# Revit family: Sanitary_Toilet-Accessories_DURAVIT-AG_ME-by-Starck-Siphon-cover-085840ed
name_source: partatom
category: Specialty Equipment
revit_build: Autodesk Revit 2018 (Build: 20190510_1515(x64)
units: mm (PartAtom-declared; Revit-internal decimal feet)

## family parameters
Cut with Voids When Loaded = No
Host = Face
OmniClass Number = 23.19.31.17
OmniClass Title = Sanitary Room Units
Part Type = Normal
Room Calculation Point = No
Round Connector Dimension = Use Diameter
Shared = No

## types (2) — shared parameters
BIMobject category = Toilet Accessories
Date of publishing = 11.01.2017 00:00:00
Default Elevation = 1219 mm
ETIM classification = EC011331 | Siphon cover
Edition number = 1
IFC Classification = Sanitary Terminal
Installation instructions = http://pro.duravit.com
Manufacturer = Duravit
Manufacturer country = France
Manufacturer name = DURAVIT AG
Masterformat 2014 Code = 22 13 19.13
Masterformat 2014 Description = Sanitary Drains
Material main = Ceramics
Model = ME by Starck Siphon cover - 085840
OmniClass Code = 23-19 31 17
OmniClass Description = Sanitary Room Units
Product Guid = 34885342-cf50-4305-ad12-78612407e65c
Product SKU = me-by-starck-siphon-cover-085840
Product certification = http://pro.duravit.com
Product data url = https://bimobject.com
Product family = ME by Starck
Product group = Siphon cover
Product name = ME by Starck Siphon cover - 085840
Product url = http://pro.duravit.com
QR code = https://bimobject.com
Technical description = http://pro.duravit.com
UNSPSC Code = 301815
URL = https://www.duravit.com
Uniclass 2015 Code = Pr_40_20_93
Uniclass 2015 Name = Urinal and WC fittings
Uniformat II Code = D2010
Uniformat II Description = Plumbing Fixtures
Weight Net (Kg) = 7
Youtube clip = http://pro.duravit.com

## per-type parameters (varying)
| type | Description | Main material |
| 00 - White Alpin | Duravit ME by Starck Siphon cover White High Gloss - 0858400000 | Duravit - Ceramic - 00 - White Alpin |
| 00 - White Alpin WonderGliss | Duravit ME by Starck Siphon cover White High Gloss , WonderGliss - 08584000001 | Duravit - Ceramic - 00 - White Alpin WonderGliss |

## geometry (parser evidence)
native form markers: Sweep x3
no freeform markers — native parametric forms only
